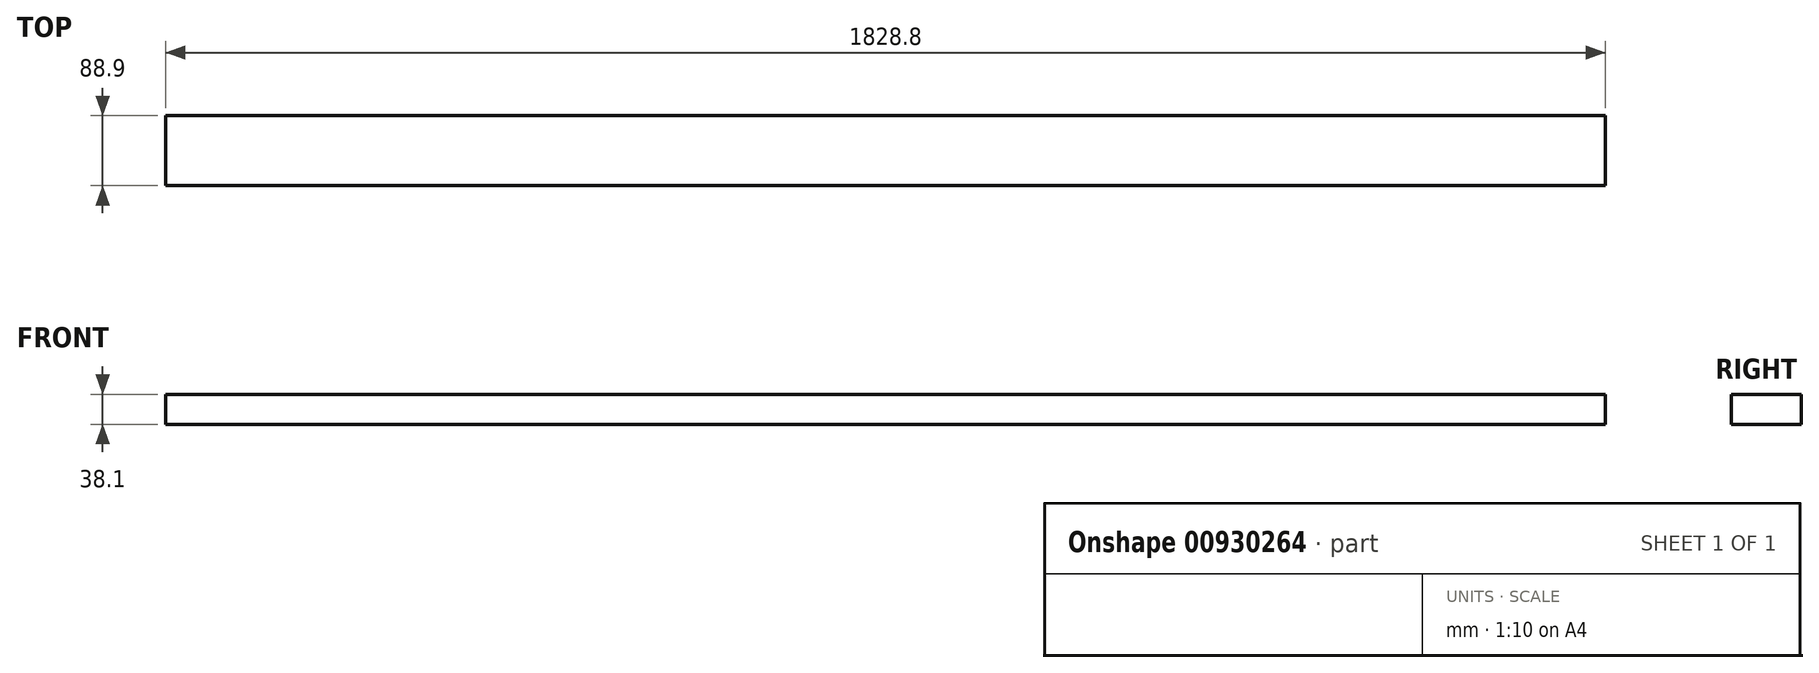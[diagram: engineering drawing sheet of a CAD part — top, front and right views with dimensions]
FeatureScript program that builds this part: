
annotation { "Feature Type Name" : "Feature", "Feature Type Description" : "" }
export const myFeature = defineFeature(function(context is Context, id is Id, definition is map)
    precondition{}
    {
        {
            var Q0;
            Q0=qCreatedBy(makeId("Right.planeOp"),FACE);
            var sketch = newSketch(context, id + "F0", { "sketchPlane" : qUnion([Q0])});
            skLineSegment(sketch, "E0.bottom", {"start": v(44.45, -19.05) * mm, "end": v(-44.45, -19.05) * mm});
            skLineSegment(sketch, "E0.top", {"start": v(44.45, 19.05) * mm, "end": v(-44.45, 19.05) * mm});
            skLineSegment(sketch, "E0.left", {"start": v(44.45, -19.05) * mm, "end": v(44.45, 19.05) * mm});
            skLineSegment(sketch, "E0.right", {"start": v(-44.45, -19.05) * mm, "end": v(-44.45, 19.05) * mm});
            skPoint(sketch, "E0.middle", {"position": v(0, 0) * mm});
            skSolve(sketch);
        }
        {
            var Q0;
            Q0=qSketchRegion(id+"F0",true);
            extrude(context, id + "F1", {"entities" : qUnion([Q0]), "endBound" : BoundingType.SYMMETRIC, "depth" : 1828.8 * mm});
        }
    });
